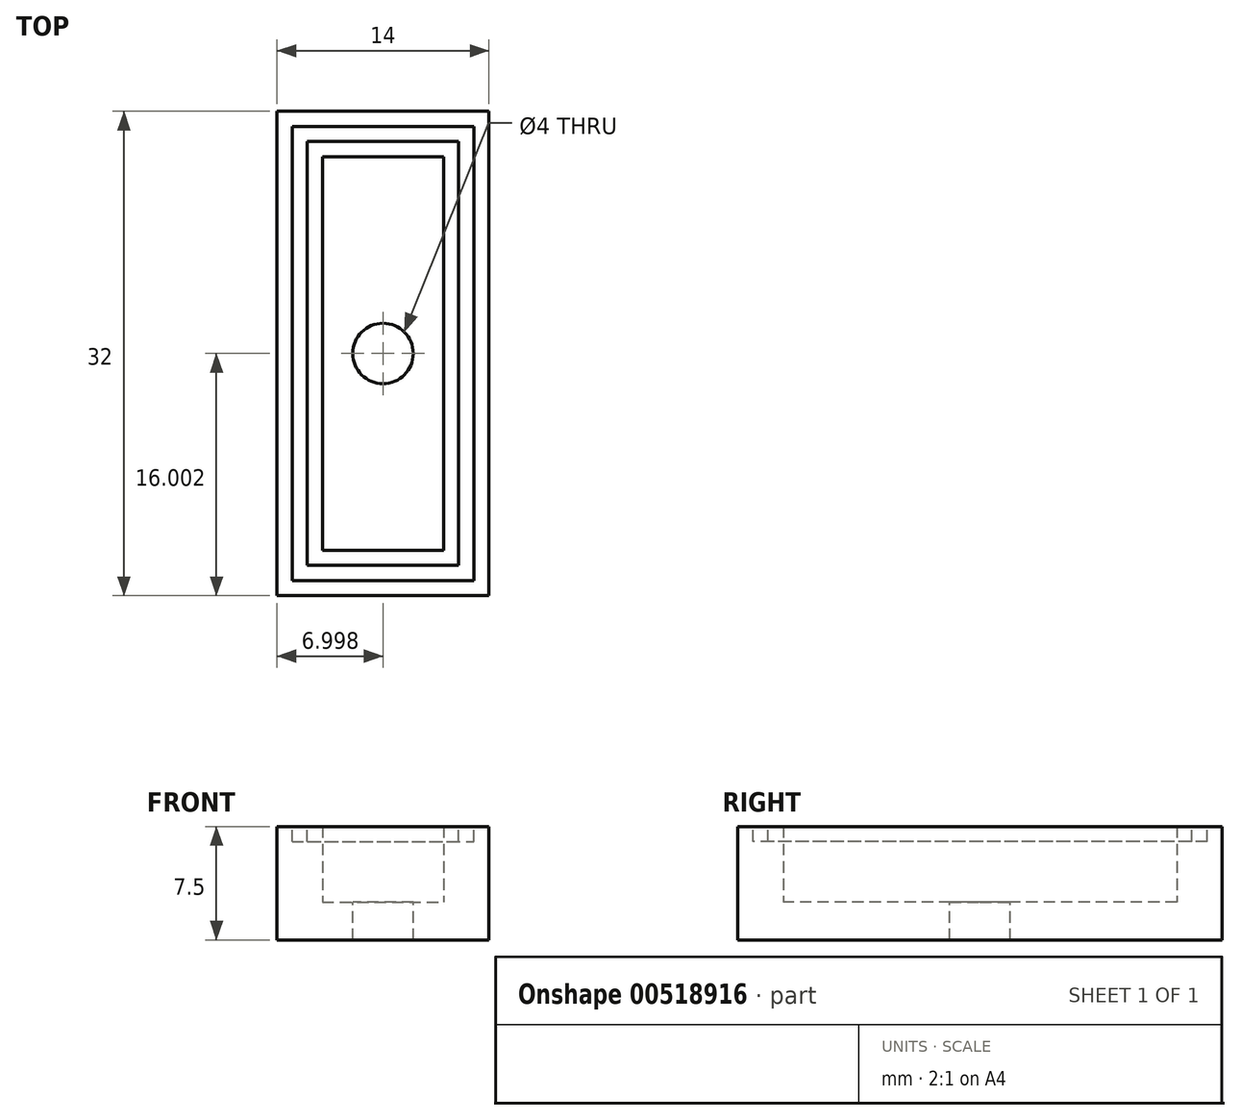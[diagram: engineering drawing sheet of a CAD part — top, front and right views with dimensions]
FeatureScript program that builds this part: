
annotation { "Feature Type Name" : "Feature", "Feature Type Description" : "" }
export const myFeature = defineFeature(function(context is Context, id is Id, definition is map)
    precondition{}
    {
        {
            var Q0;
            Q0=qCreatedBy(makeId("Top.planeOp"),FACE);
            var sketch = newSketch(context, id + "F0", { "sketchPlane" : qUnion([Q0])});
            skLineSegment(sketch, "E0.bottom", {"start": v(-0.1, 12.18) * mm, "end": v(7.9, 12.18) * mm});
            skLineSegment(sketch, "E0.top", {"start": v(-0.1, -13.82) * mm, "end": v(7.9, -13.82) * mm});
            skLineSegment(sketch, "E0.left", {"start": v(-0.1, 12.18) * mm, "end": v(-0.1, -13.82) * mm});
            skLineSegment(sketch, "E0.right", {"start": v(7.9, 12.18) * mm, "end": v(7.9, -13.82) * mm});
            skLineSegment(sketch, "E1.bottom", {"start": v(-3.1, 15.18) * mm, "end": v(10.9, 15.18) * mm});
            skLineSegment(sketch, "E1.top", {"start": v(-3.1, -16.82) * mm, "end": v(10.9, -16.82) * mm});
            skLineSegment(sketch, "E1.left", {"start": v(-3.1, 15.18) * mm, "end": v(-3.1, -16.82) * mm});
            skLineSegment(sketch, "E1.right", {"start": v(10.9, 15.18) * mm, "end": v(10.9, -16.82) * mm});
            skLineSegment(sketch, "E2", {"start": v(1.46, 15.18) * mm, "end": v(1.46, 12.18) * mm, "construction": true});
            skLineSegment(sketch, "E3", {"start": v(7.9, -0.82) * mm, "end": v(10.9, -0.82) * mm, "construction": true});
            skPoint(sketch, "E3.startSnap0", {"position": v(10.9, -0.82) * mm});
            skLineSegment(sketch, "E4", {"start": v(-0.1, -8.4) * mm, "end": v(-3.1, -8.4) * mm, "construction": true});
            skLineSegment(sketch, "E5", {"start": v(2.65, -13.82) * mm, "end": v(2.65, -16.82) * mm, "construction": true});
            skCircle(sketch, "E6", {"center": v(3.9, -0.82) * mm, "radius": 2 * mm});
            skLineSegment(sketch, "E7", {"start": v(3.9, -0.82) * mm, "end": v(3.9, -13.82) * mm, "construction": true});
            skLineSegment(sketch, "E8", {"start": v(3.9, -0.82) * mm, "end": v(7.9, -0.82) * mm, "construction": true});
            skSolve(sketch);
        }
        {
            var Q0;
            Q0=makeQuery(id+"F0.imprint","IMPRINT",FACE,{"disambiguationData":[TD([[makeQuery(id+"F0.imprint","IMPRINT",EDGE,{"derivedFrom":sQuery(id+"F0.wireOp",EDGE,"E0.bottom")}),1.0]])]});
            var Q1;
            Q1=makeQuery(id+"F0.imprint","IMPRINT",FACE,{"disambiguationData":[TD([[makeQuery(id+"F0.imprint","IMPRINT",EDGE,{"derivedFrom":sQuery(id+"F0.wireOp",EDGE,"E0.bottom")}),-1.0]])]});
            extrude(context, id + "F1", {"entities" : qUnion([Q0, Q1]), "oppositeDirection" : true, "depth" : 2.5 * mm, "offsetDistance" : 25 * mm});
        }
        {
            var Q0;
            Q0=makeQuery(id+"F0.imprint","IMPRINT",FACE,{"disambiguationData":[TD([[makeQuery(id+"F0.imprint","IMPRINT",EDGE,{"derivedFrom":sQuery(id+"F0.wireOp",EDGE,"E0.bottom")}),1.0]])]});
            extrude(context, id + "F2", {"entities" : qUnion([Q0]), "operationType" : NewBodyOperationType.ADD, "depth" : 5 * mm, "offsetDistance" : 25 * mm});
        }
        {
            var Q0;
            Q0=makeQuery(id+"F2.opExtrude","CAP_FACE",FACE,{"disambiguationData":[OSD([sQuery(id+"F0.wireOp",EDGE,"E0.bottom"),sQuery(id+"F0.wireOp",EDGE,"E0.top"),sQuery(id+"F0.wireOp",EDGE,"E0.left"),sQuery(id+"F0.wireOp",EDGE,"E0.right"),sQuery(id+"F0.wireOp",EDGE,"E1.bottom"),sQuery(id+"F0.wireOp",EDGE,"E1.top"),sQuery(id+"F0.wireOp",EDGE,"E1.left"),sQuery(id+"F0.wireOp",EDGE,"E1.right")])],"isStart":false});
            var sketch = newSketch(context, id + "F3", { "sketchPlane" : qUnion([Q0])});
            skLineSegment(sketch, "E9.bottom", {"start": v(-2.1, 14.18) * mm, "end": v(9.9, 14.18) * mm});
            skLineSegment(sketch, "E9.top", {"start": v(-2.1, -15.82) * mm, "end": v(9.9, -15.82) * mm});
            skLineSegment(sketch, "E9.left", {"start": v(-2.1, 14.18) * mm, "end": v(-2.1, -15.82) * mm});
            skLineSegment(sketch, "E9.right", {"start": v(9.9, 14.18) * mm, "end": v(9.9, -15.82) * mm});
            skLineSegment(sketch, "E10.bottom", {"start": v(-1.1, 13.18) * mm, "end": v(8.9, 13.18) * mm});
            skLineSegment(sketch, "E10.top", {"start": v(-1.1, -14.82) * mm, "end": v(8.9, -14.82) * mm});
            skLineSegment(sketch, "E10.left", {"start": v(-1.1, 13.18) * mm, "end": v(-1.1, -14.82) * mm});
            skLineSegment(sketch, "E10.right", {"start": v(8.9, 13.18) * mm, "end": v(8.9, -14.82) * mm});
            skLineSegment(sketch, "E11", {"start": v(8.9, -3.55) * mm, "end": v(9.9, -3.55) * mm, "construction": true});
            skLineSegment(sketch, "E12", {"start": v(-1.1, -4.54) * mm, "end": v(-2.1, -4.54) * mm, "construction": true});
            skLineSegment(sketch, "E13", {"start": v(3.9, -14.82) * mm, "end": v(3.9, -15.82) * mm, "construction": true});
            skSolve(sketch);
        }
        {
            var Q0;
            Q0=makeQuery(id+"F3.imprint","IMPRINT",FACE,{"disambiguationData":[TD([[makeQuery(id+"F3.imprint","IMPRINT",EDGE,{"derivedFrom":sQuery(id+"F3.wireOp",EDGE,"E9.bottom")}),-1.0]])]});
            extrude(context, id + "F4", {"entities" : qUnion([Q0]), "operationType" : NewBodyOperationType.REMOVE, "oppositeDirection" : true, "depth" : 1 * mm, "offsetDistance" : 25 * mm});
        }
    });
